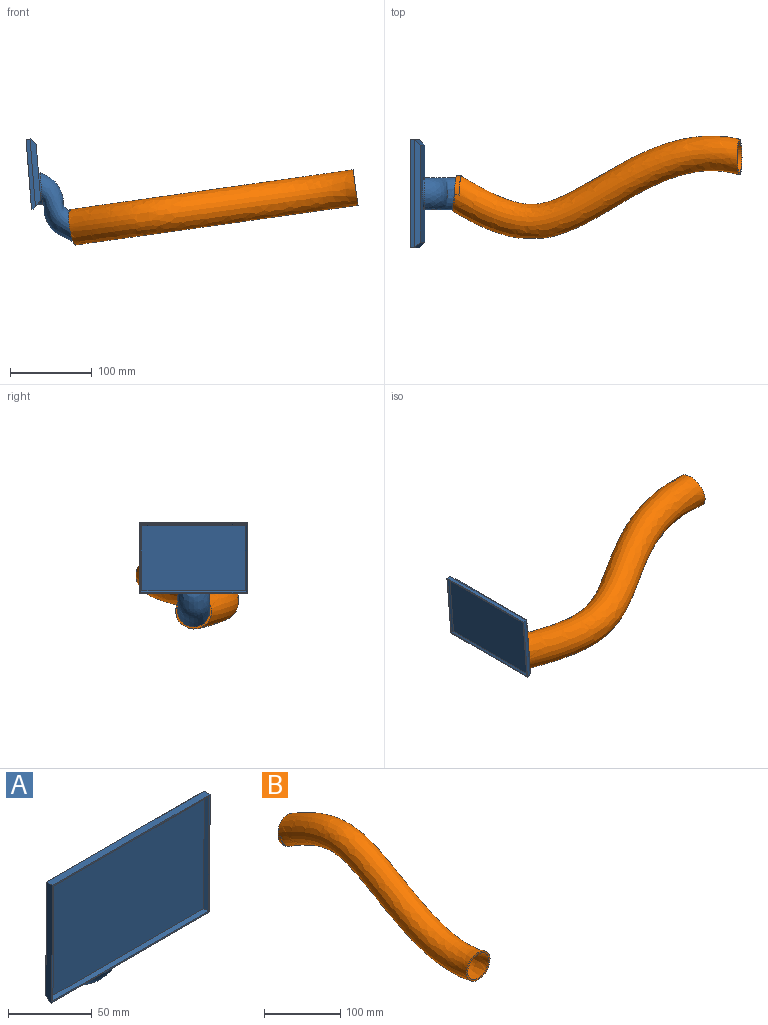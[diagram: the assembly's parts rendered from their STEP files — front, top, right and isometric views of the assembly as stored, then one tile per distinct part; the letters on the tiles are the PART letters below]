
ASSEMBLY  parts=2 mates=1
PART A: 18 faces, bbox 138.4x56.5x136.7 mm
  f0: plane 133x86mm, normal (0,-1,-0.01), area 434mm2, adj f8,f9,f10,f11,f14,f15,f16,f17
  f1: plane 44.43x44.34mm, normal (0,1,0.07), area 1194.6mm2, adj f2
  f2: bspline ~89.17x38.66mm, area 7064.7mm2, adj f1,f3
  f3: cylinder r=19.5mm len=39.04mm, axis (0,1,0.01), area 339.4mm2, adj f2,f4,f12
  f4: plane 119x69mm, normal (0,1,0.01), area 7105.8mm2, adj f3,f5,f6,f7,f12
  f5: plane 83x7.48mm, normal (0.71,0.71,0), area 752.4mm2, adj f4,f6,f10,f12
  f6: plane 133x7.04mm, normal (0,0.7,0.71), area 1247.3mm2, adj f4,f5,f7,f8
  f7: plane 83x7.48mm, normal (-0.71,0.71,0), area 752.4mm2, adj f4,f6,f9,f12
  f8: plane 133x5mm, normal (0,-0.01,1), area 665mm2, adj f0,f6,f9,f10
  f9: plane 86.03x5.53mm, normal (-1,0,0), area 425.5mm2, adj f0,f7,f8,f11,f12
  f10: plane 86.03x5.53mm, normal (1,0,0), area 425.5mm2, adj f0,f5,f8,f11,f12
  f11: plane 133x2mm, normal (0,0.01,-1), area 266mm2, adj f0,f9,f10,f12
  f12: plane 133x10.06mm, normal (0,0.71,-0.7), area 1685.1mm2, adj f3,f4,f5,f7,f9,f10,f11
  f13: plane 127x80mm, normal (0,-1,-0.01), area 10160mm2, adj f14,f15,f16,f17
  f14: plane 84x2.52mm, normal (0.71,-0.71,0), area 231.9mm2, adj f0,f13,f15,f16
  f15: plane 131x2.01mm, normal (0,-0.7,-0.71), area 364.9mm2, adj f0,f13,f14,f17
  f16: plane 131x2.01mm, normal (0,-0.71,0.7), area 364.9mm2, adj f0,f13,f14,f17
  f17: plane 84x2.52mm, normal (-0.71,-0.71,0), area 231.9mm2, adj f0,f13,f15,f16
PART B: 13 faces, bbox 99x367x138.4 mm
  f0: bspline ~355.29x122.47mm, area 44836.4mm2, adj f3,f4,f9,f10,f11
  f1: plane 10.69x0.88mm, normal (0,0.96,-0.27), area 4.4mm2, adj f2,f5
  f2: bspline ~355.97x127.39mm, area 50853.2mm2, adj f1,f3,f5,f6,f12
  f3: plane 49.43x49.43mm, normal (0,-1,0), area 325.9mm2, adj f0,f2
  f4: plane 50x30.5mm, normal (0,0.96,-0.27), area 23.3mm2, adj f0,f8
  f5: plane 48.26x27.84mm, normal (0,-1,0), area 61.7mm2, adj f1,f2,f6
  f6: cylinder r=22mm len=44mm, axis (0,1,0), area 410mm2, adj f2,f5,f7
  f7: plane 44x44mm, normal (0,1,0), area 325.9mm2, adj f6,f8,f11,f12
  f8: cylinder r=19.5mm len=39mm, axis (0,1,0), area 0mm2, adj f4,f7
  f9: cylinder r=22mm len=34.05mm, axis (0,1,0), area 0mm2, adj f0,f10
  f10: plane 39.29x20.71mm, normal (0,-1,0), area 120.1mm2, adj f0,f9,f11
  f11: cylinder r=19.5mm len=39mm, axis (0,1,0), area 346.1mm2, adj f0,f7,f10
  f12: cylinder r=22mm len=44mm, axis (0,-1,0), area 0mm2, adj f2,f7
PLACE A rot(axis=(0.04,-0.04,-1),90.1deg) t=(-608.32,-1.33,152.02)mm
PLACE B rot(axis=(0.52,-0.6,0.6),124.7deg) t=(-608.3,-1.33,151.88)mm
MATE fastened A.f1 <-> B.f8  axis (0.99,0,0.14) through (-608.3,-1.33,151.88)mm
